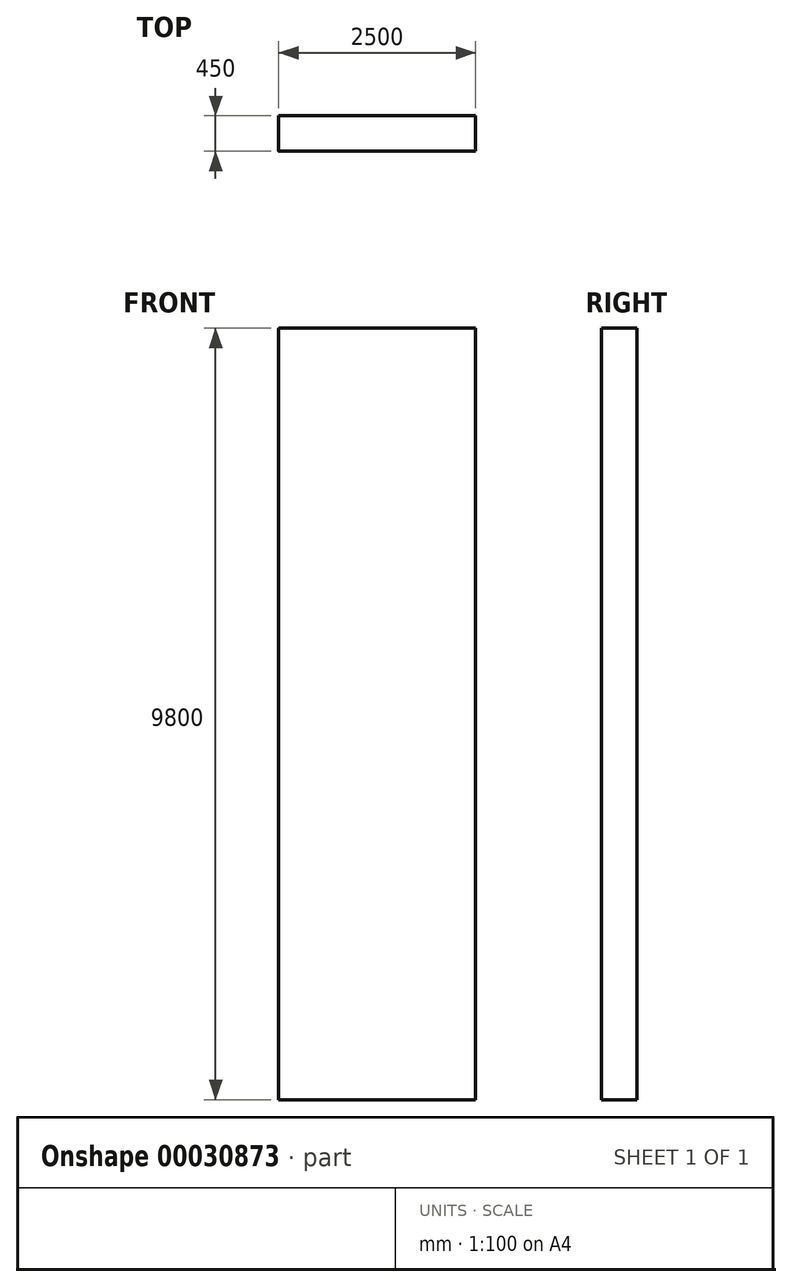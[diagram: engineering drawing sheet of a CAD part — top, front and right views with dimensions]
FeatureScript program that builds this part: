
annotation { "Feature Type Name" : "Feature", "Feature Type Description" : "" }
export const myFeature = defineFeature(function(context is Context, id is Id, definition is map)
    precondition{}
    {
        {
            var Q0;
            Q0=qCreatedBy(makeId("Front.planeOp"),FACE);
            var sketch = newSketch(context, id + "F0", { "sketchPlane" : qUnion([Q0])});
            skLineSegment(sketch, "E0.bottom", {"start": v(1249.79, -1127.53) * mm, "end": v(-1250.21, -1127.53) * mm});
            skLineSegment(sketch, "E0.top", {"start": v(1249.79, 8672.47) * mm, "end": v(-1243.86, 8672.47) * mm});
            skLineSegment(sketch, "E0.left", {"start": v(1249.79, -1127.53) * mm, "end": v(1249.79, 8672.47) * mm});
            skLineSegment(sketch, "E0.right", {"start": v(-1250.21, -1127.53) * mm, "end": v(-1250.21, 8666.12) * mm});
            skPoint(sketch, "E1.visualSharp", {"position": v(-1250.21, 8672.47) * mm});
            skArc(sketch, "E1.filletArc", {"start": v(-1243.86, 8672.47) * mm, "mid": v(-1248.35, 8670.6) * mm, "end": v(-1250.21, 8666.12) * mm});
            skSolve(sketch);
        }
        {
            var Q0;
            Q0 = qSketchRegion(id + "F0", true);
            extrude(context, id + "F1", {"entities" : qUnion([Q0]), "depth" : 450 * mm});
        }
    });
